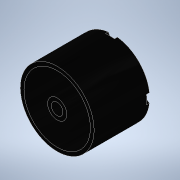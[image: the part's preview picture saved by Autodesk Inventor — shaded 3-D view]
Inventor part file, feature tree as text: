
AUTODESK INVENTOR PART (.ipt)
format: ipt  version: 2022 (Build 260153000, 153)  size: 240,128 bytes
history: native  units: in
note: dims shown in document units (in); Inventor stores cm internally (conversion verified against a paired STEP export)
features: sketch x2, revolve x1, extrude x1, shell x1
ambient origin geometry x8: Origin, YZ Plane, XZ Plane, XY Plane, X Axis, Y Axis, Z Axis, Center Point
bodies: Solid1 (feature_tree)
feature tree (5):
  revolve  "Revolution1"  [1 undecoded]
  extrude  "Extrusion1"  Depth=0.1969in
  shell  "Shell1"  Thickness=0.5512in
  sketch  "Sketch1"  dims[d0=1.2402in d1=2.2047in]
  sketch  "Sketch2"  dims[d2=0.2756in d3=0.0591in d4=0.5512in d5=0.1969in d6=90.0deg d7=0.1531in d8=1.1811in d9=0.9055in d10=0.1575in d11=1.5748in d13=360.0deg d15=0.4331in d16=0.0in d17=0.125in]
note: 1 required parameter value undecoded (feature->parameter linkage not recoverable at this tier; creation-order binding heuristic only, values carry confidence <= 0.55)
